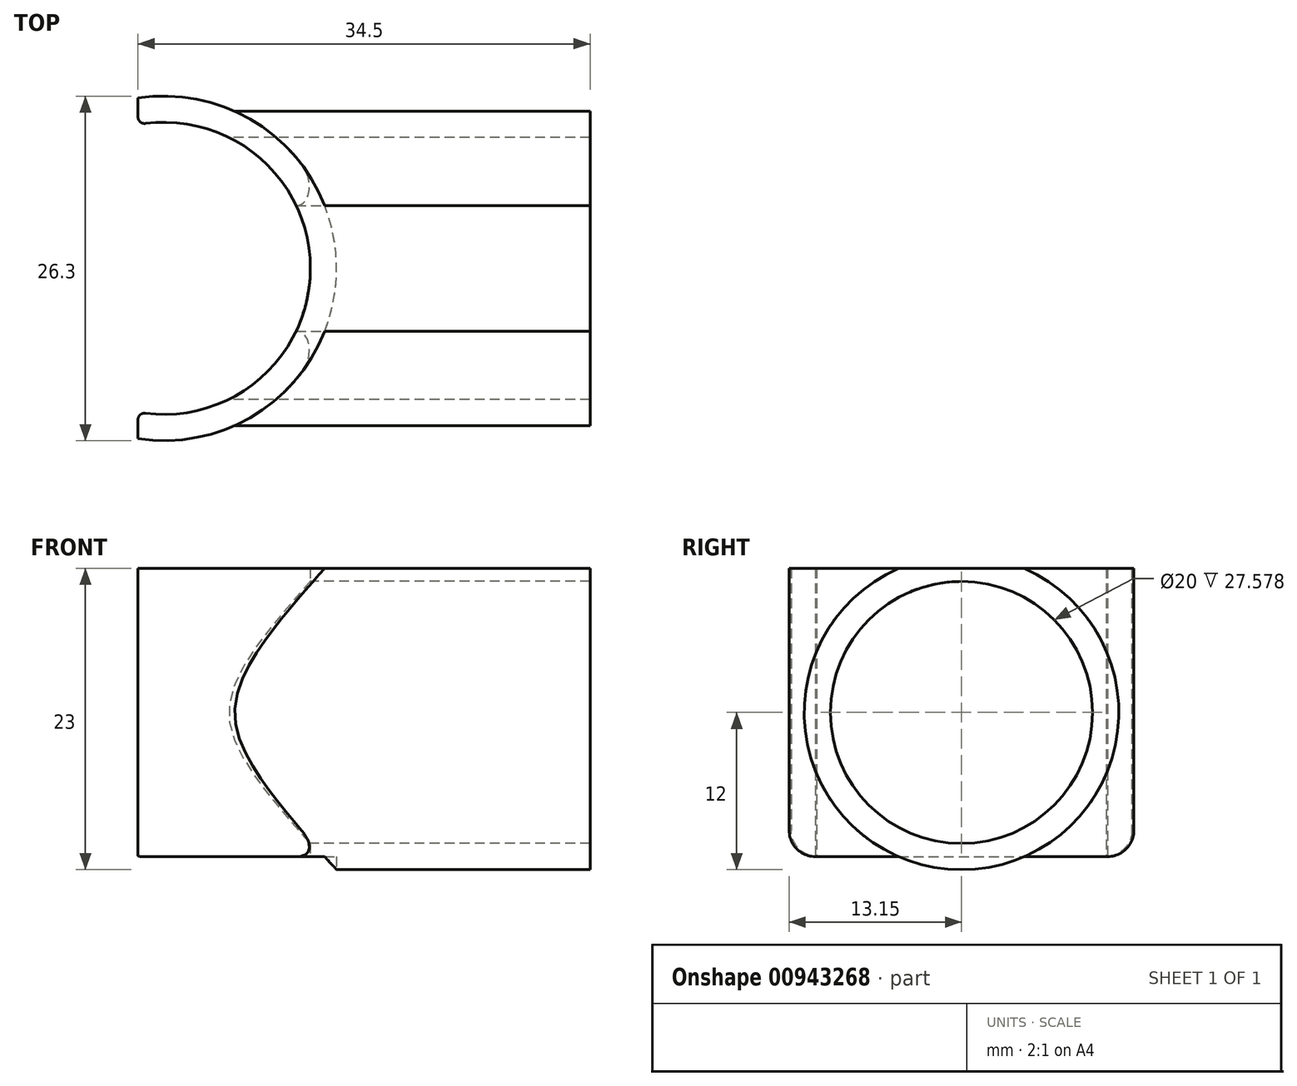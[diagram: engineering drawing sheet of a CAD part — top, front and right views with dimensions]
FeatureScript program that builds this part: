
annotation { "Feature Type Name" : "Feature", "Feature Type Description" : "" }
export const myFeature = defineFeature(function(context is Context, id is Id, definition is map)
    precondition{}
    {
        {
            var Q0;
            Q0=qCreatedBy(makeId("Top.planeOp"),FACE);
            var sketch = newSketch(context, id + "F0", { "sketchPlane" : qUnion([Q0])});
            skCircle(sketch, "E0", {"center": v(0, 0) * mm, "radius": 11.15 * mm, "construction": true});
            skArc(sketch, "E1", {"start": v(-1.44, -11.06) * mm, "mid": v(11.15, 0) * mm, "end": v(-1.44, 11.06) * mm});
            skLineSegment(sketch, "E2", {"start": v(-2, 10.97) * mm, "end": v(-2, -10.97) * mm, "construction": true});
            skArc(sketch, "E3", {"start": v(-2, -13) * mm, "mid": v(13.15, 0) * mm, "end": v(-2, 13) * mm});
            skLineSegment(sketch, "E4", {"start": v(-2, 11.55) * mm, "end": v(-2, 13) * mm});
            skLineSegment(sketch, "E5", {"start": v(-2, -11.55) * mm, "end": v(-2, -13) * mm});
            skPoint(sketch, "E6.visualSharp", {"position": v(-2, 10.97) * mm});
            skArc(sketch, "E6.filletArc", {"start": v(-2, 11.55) * mm, "mid": v(-1.83, 11.18) * mm, "end": v(-1.44, 11.06) * mm});
            skPoint(sketch, "E7.visualSharp", {"position": v(-2, -10.97) * mm});
            skArc(sketch, "E7.filletArc", {"start": v(-1.44, -11.06) * mm, "mid": v(-1.83, -11.18) * mm, "end": v(-2, -11.55) * mm});
            skSolve(sketch);
        }
        {
            var Q0;
            Q0 = qSketchRegion(id + "F0", true);
            extrude(context, id + "F1", {"entities" : qUnion([Q0]), "depth" : 11 * mm, "offsetDistance" : 25 * mm, "hasSecondDirection" : true, "secondDirectionOppositeDirection" : true, "secondDirectionDepth" : 11 * mm});
        }
        {
            var Q0;
            Q0=qCreatedBy(makeId("Right.planeOp"),FACE);
            var sketch = newSketch(context, id + "F2", { "sketchPlane" : qUnion([Q0])});
            skCircle(sketch, "E8", {"center": v(0, 0) * mm, "radius": 10 * mm});
            skSolve(sketch);
        }
        {
            var Q0;
            Q0 = qSketchRegion(id + "F2", true);
            extrude(context, id + "F3", {"entities" : qUnion([Q0]), "operationType" : NewBodyOperationType.REMOVE, "depth" : 25 * mm, "offsetDistance" : 25 * mm});
        }
        {
            var Q0;
            Q0=qCreatedBy(makeId("Right.planeOp"),FACE);
            cPlane(context, id + "F4", {"entities" : qUnion([Q0]), "cplaneType" : CPlaneType.OFFSET, "offset" : 32.5 * mm, "width" : 150 * mm, "height" : 150 * mm});
        }
        {
            var Q0;
            Q0=qCreatedBy(id+"F4.planeOp",FACE);
            var sketch = newSketch(context, id + "F5", { "sketchPlane" : qUnion([Q0])});
            skCircle(sketch, "E9", {"center": v(0, 0) * mm, "radius": 10 * mm});
            skCircle(sketch, "E10", {"center": v(0, 0) * mm, "radius": 12 * mm});
            skSolve(sketch);
        }
        {
            var Q0;
            Q0 = qSketchRegion(id + "F5", true);
            var Q1;
            Q1=makeQuery(id+"F1.opExtrude","SWEPT_FACE",FACE,{"disambiguationData":[OSD([sQuery(id+"F0.wireOp",EDGE,"E3")])]});
            extrude(context, id + "F6", {"entities" : qUnion([Q0]), "operationType" : NewBodyOperationType.ADD, "endBound" : BoundingType.UP_TO_SURFACE, "oppositeDirection" : true, "depth" : 25 * mm, "endBoundEntityFace" : qUnion([Q1]), "offsetDistance" : 25 * mm});
        }
        {
            var Q0;
            {var subQ0=sQuery(id+"F0.wireOp",EDGE,"E3");Q0=makeQuery(id+"F6.boolean.opBoolean","SPLIT",EDGE,{"disambiguationData":[topologyDisambiguationEdgeConnected([makeQuery(id+"F1.opExtrude","CAP_FACE",FACE,{"disambiguationData":[OSD([sQuery(id+"F0.wireOp",EDGE,"E1"),subQ0,sQuery(id+"F0.wireOp",EDGE,"E4"),sQuery(id+"F0.wireOp",EDGE,"E5"),sQuery(id+"F0.wireOp",EDGE,"E6.filletArc"),sQuery(id+"F0.wireOp",EDGE,"E7.filletArc")])],"isStart":true}),makeQuery(id+"F6.opExtrude","CAP_FACE",FACE,{"disambiguationData":[OSD([sQuery(id+"F5.wireOp",EDGE,"E9"),sQuery(id+"F5.wireOp",EDGE,"E10")])],"isStart":false})])],"derivedFrom":makeQuery(id+"F1.opExtrude","CAP_EDGE",EDGE,{"disambiguationData":[OSD([subQ0])],"isStart":true})});}
            fillet(context, id + "F7", {"entities" : qUnion([Q0]), "radius" : 2 * mm, "tangentPropagation" : true, "allowEdgeOverflow" : false});
        }
        {
            var Q0;
            Q0=qCreatedBy(makeId("Right.planeOp"),FACE);
            var sketch = newSketch(context, id + "F8", { "sketchPlane" : qUnion([Q0])});
            skLineSegment(sketch, "E11.bottom", {"start": v(8.33, 11) * mm, "end": v(-7.37, 11) * mm});
            skLineSegment(sketch, "E11.top", {"start": v(8.33, 16.17) * mm, "end": v(-7.37, 16.17) * mm});
            skLineSegment(sketch, "E11.left", {"start": v(8.33, 11) * mm, "end": v(8.33, 16.17) * mm});
            skLineSegment(sketch, "E11.right", {"start": v(-7.37, 11) * mm, "end": v(-7.37, 16.17) * mm});
            skSolve(sketch);
        }
        {
            var Q0;
            Q0 = qSketchRegion(id + "F8", true);
            extrude(context, id + "F9", {"entities" : qUnion([Q0]), "operationType" : NewBodyOperationType.REMOVE, "endBound" : BoundingType.THROUGH_ALL, "depth" : 25 * mm, "offsetDistance" : 25 * mm});
        }
    });
